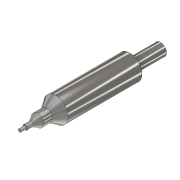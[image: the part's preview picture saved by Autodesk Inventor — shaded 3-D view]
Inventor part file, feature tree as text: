
AUTODESK INVENTOR PART (.ipt)
format: ipt  version: 2017 (Build 210142000, 142)  size: 108,544 bytes
history: native  units: mm
features: revolve x1, sketch x1
ambient origin geometry x8: Origin, YZ Plane, XZ Plane, XY Plane, X Axis, Y Axis, Z Axis, Center Point
bodies: Solid1 (feature_tree)
feature tree (2):
  revolve  "Revolution1"  [1 undecoded]
  sketch  "Sketch1"  dims[d7=5.0mm d10=12.0mm d14=1.0mm d17=1.5mm d18=3.0mm d19=1.0mm d21=0.5mm d22=0.8mm d23=2.0mm d24=4.0mm d25=2.0mm d26=90.0deg]
note: 1 required parameter value undecoded (feature->parameter linkage not recoverable at this tier; creation-order binding heuristic only, values carry confidence <= 0.55)
